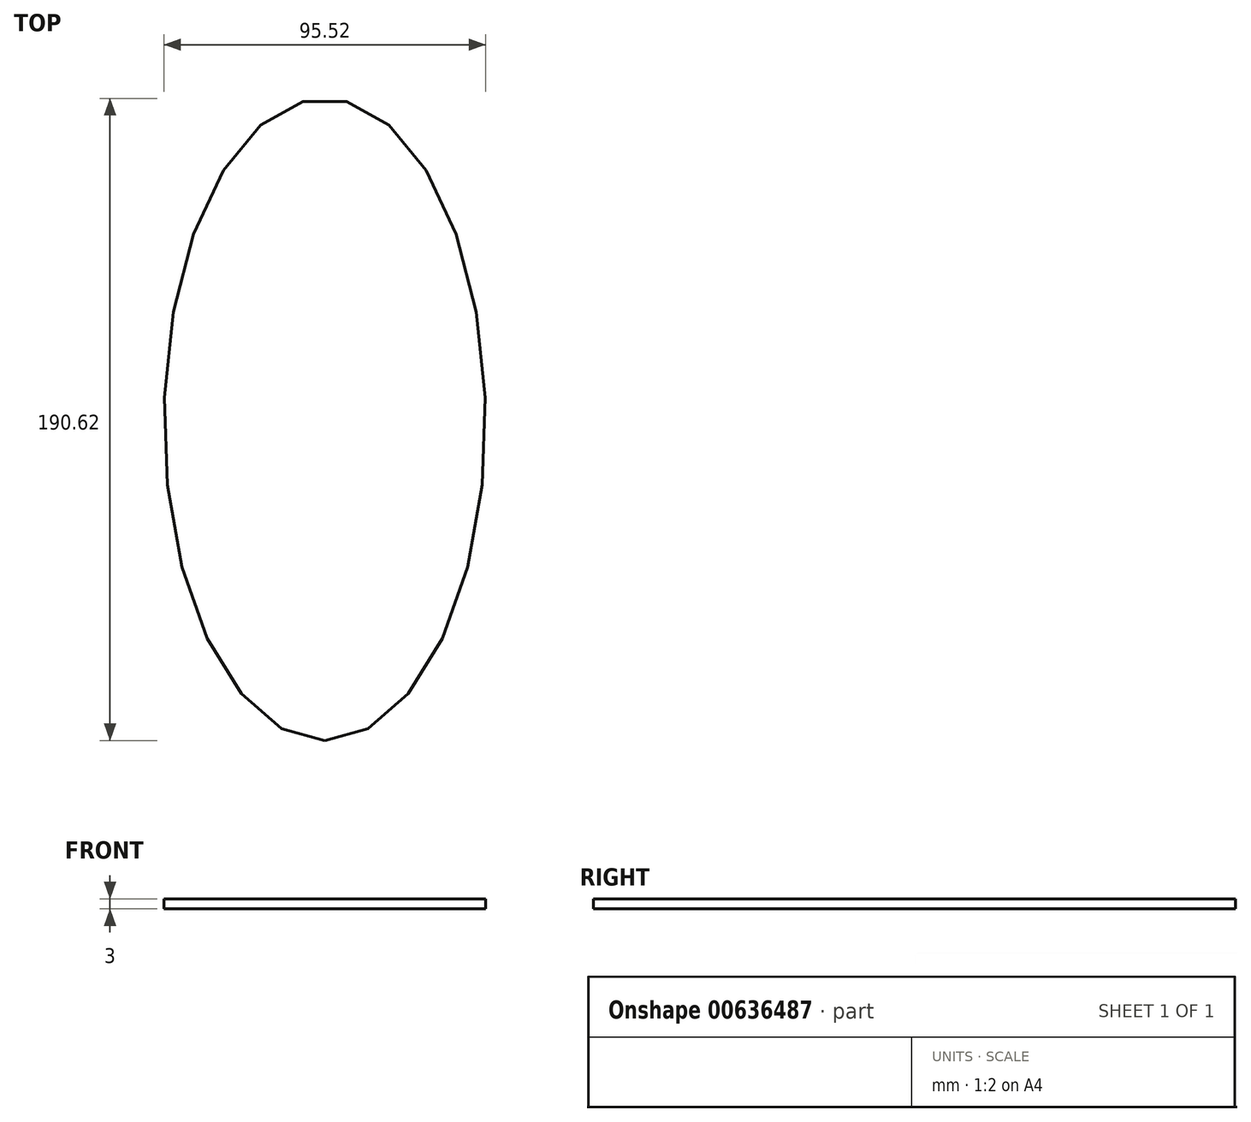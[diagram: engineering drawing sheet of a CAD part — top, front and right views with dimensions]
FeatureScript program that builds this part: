
annotation { "Feature Type Name" : "Feature", "Feature Type Description" : "" }
export const myFeature = defineFeature(function(context is Context, id is Id, definition is map)
    precondition{}
    {
        {
            var Q0;
            Q0=qCreatedBy(makeId("Top.planeOp"),FACE);
            var sketch = newSketch(context, id + "F0", { "sketchPlane" : qUnion([Q0])});
            skEllipse(sketch, "E0", {"center": v(0, 0) * mm, "majorRadius": 95.3 * mm, "minorRadius": 47.76 * mm, "majorAxis": v(0, -1)});
            skSolve(sketch);
        }
        {
            var Q0;
            Q0=makeQuery(id+"F0.imprint","IMPRINT",FACE,{"disambiguationData":[TD([[makeQuery(id+"F0.imprint","IMPRINT",EDGE,{"derivedFrom":sQuery(id+"F0.wireOp",EDGE,"E0")}),1.0]])]});
            extrude(context, id + "F1", {"entities" : qUnion([Q0]), "oppositeDirection" : true, "depth" : 3 * mm, "offsetDistance" : 25 * mm});
        }
    });
